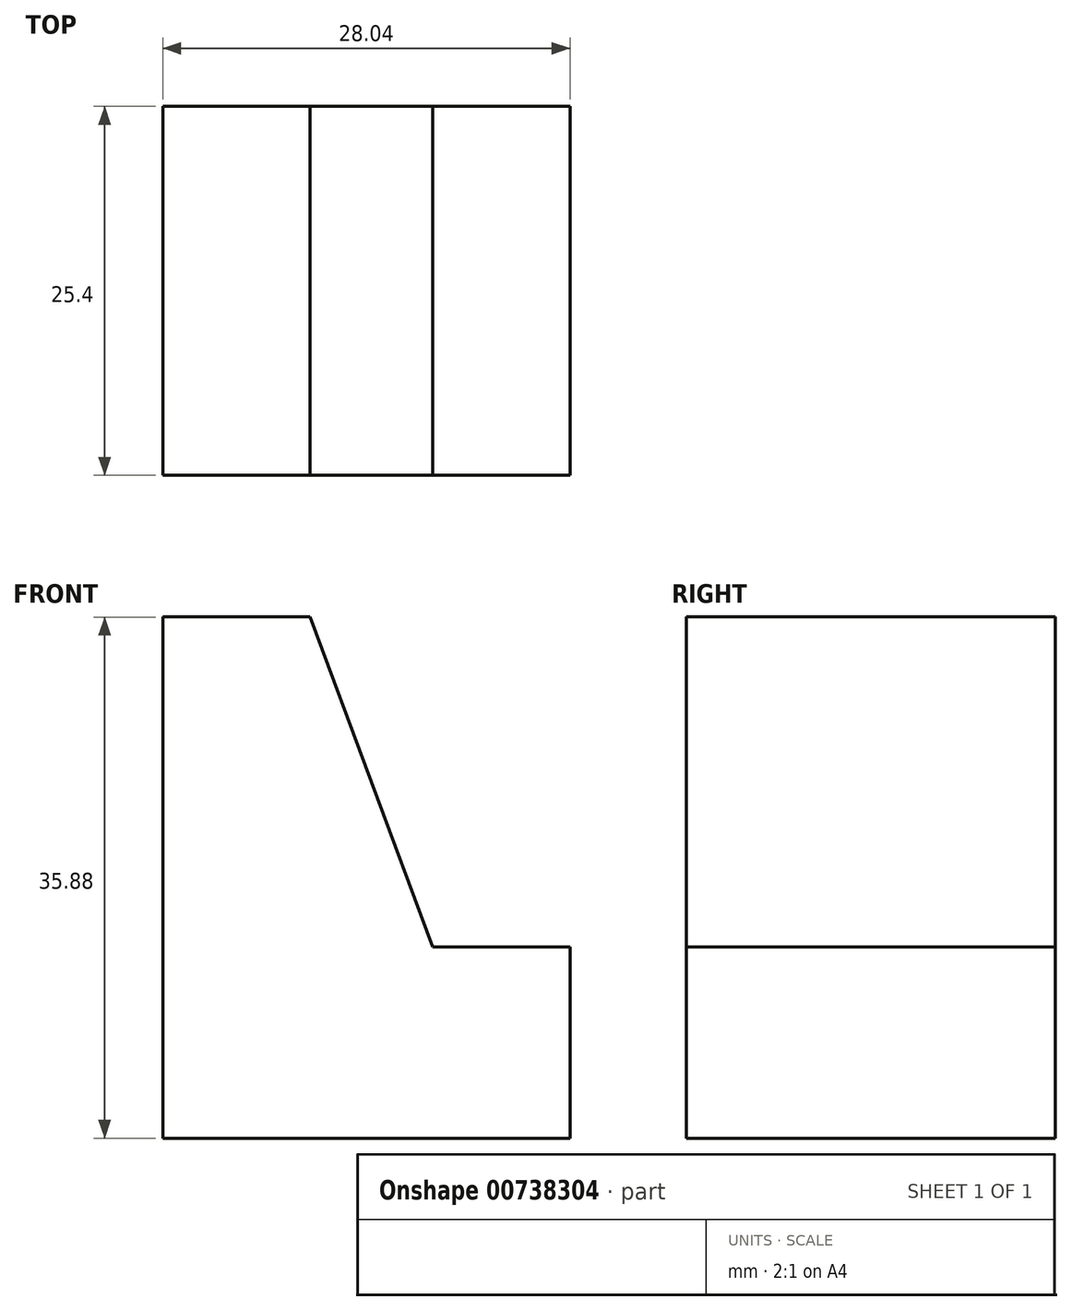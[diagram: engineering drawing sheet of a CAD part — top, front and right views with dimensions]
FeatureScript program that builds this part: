
annotation { "Feature Type Name" : "Feature", "Feature Type Description" : "" }
export const myFeature = defineFeature(function(context is Context, id is Id, definition is map)
    precondition{}
    {
        {
            var Q0;
            Q0=qCreatedBy(makeId("Front.planeOp"),FACE);
            var sketch = newSketch(context, id + "F0", { "sketchPlane" : qUnion([Q0])});
            skLineSegment(sketch, "E0", {"start": v(0, 0) * mm, "end": v(0, 35.88) * mm});
            skLineSegment(sketch, "E1", {"start": v(0, 35.88) * mm, "end": v(37.5, 35.88) * mm});
            skLineSegment(sketch, "E2", {"start": v(37.5, 35.88) * mm, "end": v(37.5, 0) * mm});
            skLineSegment(sketch, "E3", {"start": v(37.5, 0) * mm, "end": v(0, 0) * mm});
            skSolve(sketch);
        }
        {
            var Q0;
            Q0=makeQuery(id+"F0.imprint","IMPRINT",FACE,{"disambiguationData":[TD([[makeQuery(id+"F0.imprint","IMPRINT",EDGE,{"derivedFrom":sQuery(id+"F0.wireOp",EDGE,"E0")}),-1.0]])]});
            extrude(context, id + "F1", {"entities" : qUnion([Q0]), "depth" : 25.4 * mm, "offsetDistance" : 25.4 * mm});
        }
        {
            var Q0;
            Q0=makeQuery(id+"F1.opExtrude","CAP_FACE",FACE,{"disambiguationData":[OSD([sQuery(id+"F0.wireOp",EDGE,"E0"),sQuery(id+"F0.wireOp",EDGE,"E1"),sQuery(id+"F0.wireOp",EDGE,"E2"),sQuery(id+"F0.wireOp",EDGE,"E3")])],"isStart":false});
            var sketch = newSketch(context, id + "F2", { "sketchPlane" : qUnion([Q0])});
            skLineSegment(sketch, "E4", {"start": v(10.15, 35.88) * mm, "end": v(18.6, 13.17) * mm});
            skLineSegment(sketch, "E5", {"start": v(18.6, 13.17) * mm, "end": v(37.5, 13.17) * mm});
            skSolve(sketch);
        }
        {
            var Q0;
            {var subQ0=sQuery(id+"F2.wireOp",EDGE,"E4");Q0=makeQuery(id+"F2.imprint","IMPRINT",FACE,{"disambiguationData":[TD([[makeQuery(id+"F2.imprint","IMPRINT",EDGE,{"derivedFrom":subQ0}),1.0]])]});}
            extrude(context, id + "F3", {"entities" : qUnion([Q0]), "operationType" : NewBodyOperationType.REMOVE, "oppositeDirection" : true, "depth" : 25.4 * mm, "offsetDistance" : 25.4 * mm});
        }
        {
            var Q0;
            Q0=makeQuery(id+"F1.opExtrude","CAP_FACE",FACE,{"disambiguationData":[OSD([sQuery(id+"F0.wireOp",EDGE,"E0"),sQuery(id+"F0.wireOp",EDGE,"E1"),sQuery(id+"F0.wireOp",EDGE,"E2"),sQuery(id+"F0.wireOp",EDGE,"E3")])],"isStart":false});
            var sketch = newSketch(context, id + "F4", { "sketchPlane" : qUnion([Q0])});
            skLineSegment(sketch, "E6", {"start": v(28.04, 13.17) * mm, "end": v(28.04, 0) * mm});
            skSolve(sketch);
        }
        {
            var Q0;
            {var subQ0=sQuery(id+"F4.wireOp",EDGE,"E6");Q0=makeQuery(id+"F4.imprint","IMPRINT",FACE,{"disambiguationData":[TD([[makeQuery(id+"F4.imprint","IMPRINT",EDGE,{"derivedFrom":subQ0}),1.0]])]});}
            extrude(context, id + "F5", {"entities" : qUnion([Q0]), "operationType" : NewBodyOperationType.REMOVE, "oppositeDirection" : true, "depth" : 25.4 * mm, "offsetDistance" : 25.4 * mm});
        }
    });
